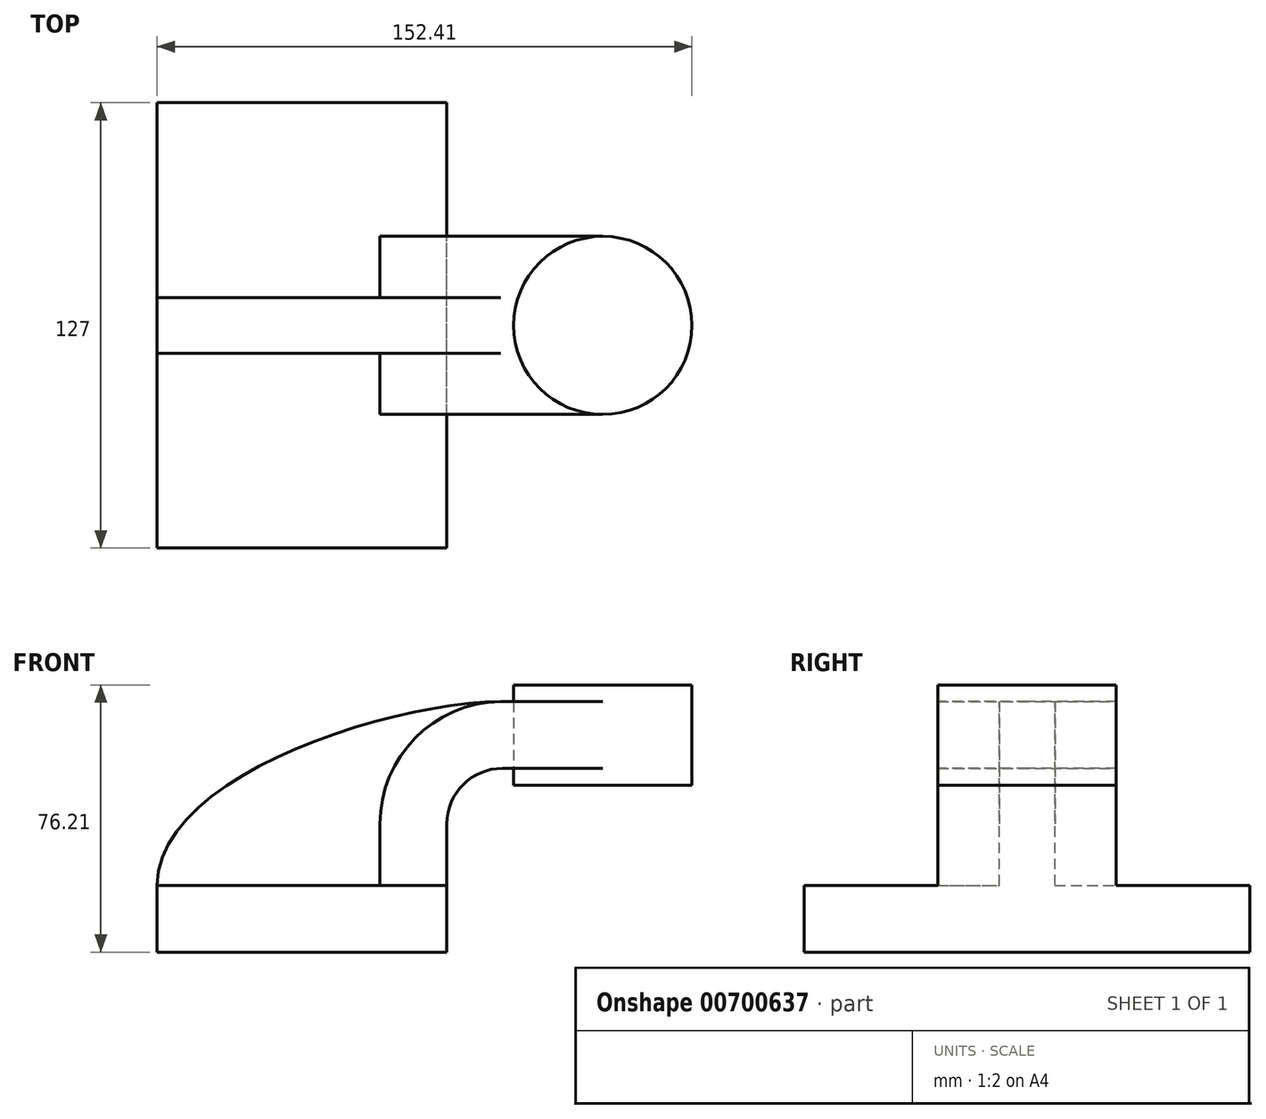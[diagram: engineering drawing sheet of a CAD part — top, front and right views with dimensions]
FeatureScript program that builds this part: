
annotation { "Feature Type Name" : "Feature", "Feature Type Description" : "" }
export const myFeature = defineFeature(function(context is Context, id is Id, definition is map)
    precondition{}
    {
        {
            var Q0;
            Q0=qCreatedBy(makeId("Front.planeOp"),FACE);
            var sketch = newSketch(context, id + "F0", { "sketchPlane" : qUnion([Q0])});
            skLineSegment(sketch, "E0.bottom", {"start": v(41.27, 9.53) * mm, "end": v(-41.28, 9.53) * mm});
            skLineSegment(sketch, "E0.top", {"start": v(41.28, -9.52) * mm, "end": v(-41.27, -9.52) * mm});
            skLineSegment(sketch, "E0.left", {"start": v(41.27, 9.53) * mm, "end": v(41.28, -9.52) * mm});
            skLineSegment(sketch, "E0.right", {"start": v(-41.28, 9.53) * mm, "end": v(-41.27, -9.52) * mm});
            skPoint(sketch, "E0.middle", {"position": v(0, 0) * mm});
            skLineSegment(sketch, "E1", {"start": v(41.27, 9.53) * mm, "end": v(41.27, 27) * mm});
            skLineSegment(sketch, "E2.bottom", {"start": v(60.32, 38.1) * mm, "end": v(111.12, 38.1) * mm});
            skLineSegment(sketch, "E2.top", {"start": v(60.32, 66.68) * mm, "end": v(111.12, 66.68) * mm});
            skLineSegment(sketch, "E2.left", {"start": v(60.32, 38.1) * mm, "end": v(60.32, 66.68) * mm});
            skLineSegment(sketch, "E2.right", {"start": v(111.12, 38.1) * mm, "end": v(111.12, 66.68) * mm});
            skPoint(sketch, "E2.middle", {"position": v(85.72, 52.39) * mm});
            skArc(sketch, "E3", {"start": v(41.27, 27) * mm, "mid": v(45.92, 38.23) * mm, "end": v(57.15, 42.88) * mm});
            skLineSegment(sketch, "E4", {"start": v(57.15, 42.88) * mm, "end": v(85.72, 42.88) * mm});
            skLineSegment(sketch, "E5.0", {"start": v(57.15, 61.93) * mm, "end": v(85.72, 61.93) * mm});
            skArc(sketch, "E5.1", {"start": v(22.22, 27) * mm, "mid": v(32.45, 51.7) * mm, "end": v(57.15, 61.93) * mm});
            skLineSegment(sketch, "E5.2", {"start": v(22.22, 9.53) * mm, "end": v(22.22, 27) * mm});
            skFitSpline(sketch, "E6", {"points": [v(-41.28, 9.52) * mm, v(57.15, 61.93) * mm], "startDerivative": vector(0.78, 94.11) * mm, "endDerivative": vector(96.63, 0.45) * mm});
            skLineSegment(sketch, "E7", {"start": v(85.72, 38.1) * mm, "end": v(85.72, 66.68) * mm});
            skSolve(sketch);
        }
        {
            var Q0;
            Q0=makeQuery(id+"F0.imprint","IMPRINT",FACE,{"disambiguationData":[TD([[makeQuery(id+"F0.imprint","IMPRINT",EDGE,{"derivedFrom":sQuery(id+"F0.wireOp",EDGE,"E0.top")}),-1.0]])]});
            extrude(context, id + "F1", {"entities" : qUnion([Q0]), "endBound" : BoundingType.SYMMETRIC, "depth" : 127 * mm, "offsetDistance" : 25.4 * mm});
        }
        {
            var Q0;
            {var subQ6=sQuery(id+"F0.wireOp",EDGE,"E1");Q0=makeQuery(id+"F0.imprint","IMPRINT",FACE,{"disambiguationData":[TD([[makeQuery(id+"F0.imprint","IMPRINT",EDGE,{"derivedFrom":subQ6}),1.0]])]});}
            var Q1;
            {var subQ0=sQuery(id+"F0.wireOp",EDGE,"E4");var subQ1=sQuery(id+"F0.wireOp",EDGE,"E2.left");var subQ2=makeQuery(id+"F0.imprint","INTERSECT",VERTEX,{"derivedFrom":[subQ1,subQ0]});Q1=makeQuery(id+"F0.imprint","IMPRINT",FACE,{"disambiguationData":[TD([[makeQuery(id+"F0.imprint","IMPRINT",EDGE,{"disambiguationData":[TD([[subQ2,-1.0]])],"derivedFrom":subQ1}),-1.0]])]});}
            extrude(context, id + "F2", {"entities" : qUnion([Q0, Q1]), "operationType" : NewBodyOperationType.ADD, "endBound" : BoundingType.SYMMETRIC, "depth" : 50.8 * mm, "offsetDistance" : 25.4 * mm});
        }
        {
            var Q0;
            {var subQ3=sQuery(id+"F0.wireOp",EDGE,"E5.2");Q0=makeQuery(id+"F0.imprint","IMPRINT",FACE,{"disambiguationData":[TD([[makeQuery(id+"F0.imprint","IMPRINT",EDGE,{"derivedFrom":subQ3}),1.0]])]});}
            extrude(context, id + "F3", {"entities" : qUnion([Q0]), "operationType" : NewBodyOperationType.ADD, "endBound" : BoundingType.SYMMETRIC, "depth" : 15.88 * mm, "offsetDistance" : 25.4 * mm});
        }
        {
            var Q0;
            {var subQ0=sQuery(id+"F0.wireOp",EDGE,"E2.right");Q0=makeQuery(id+"F0.imprint","IMPRINT",FACE,{"disambiguationData":[TD([[makeQuery(id+"F0.imprint","IMPRINT",EDGE,{"derivedFrom":subQ0}),1.0]])]});}
            var Q1;
            Q1=sQuery(id+"F0.wireOp",EDGE,"E7");
            revolve(context, id + "F4", {"surfaceOperationType" : NewSurfaceOperationType.NEW, "entities" : qUnion([Q0]), "axis" : qUnion([Q1]), "revolveType" : RevolveType.FULL});
        }
    });
